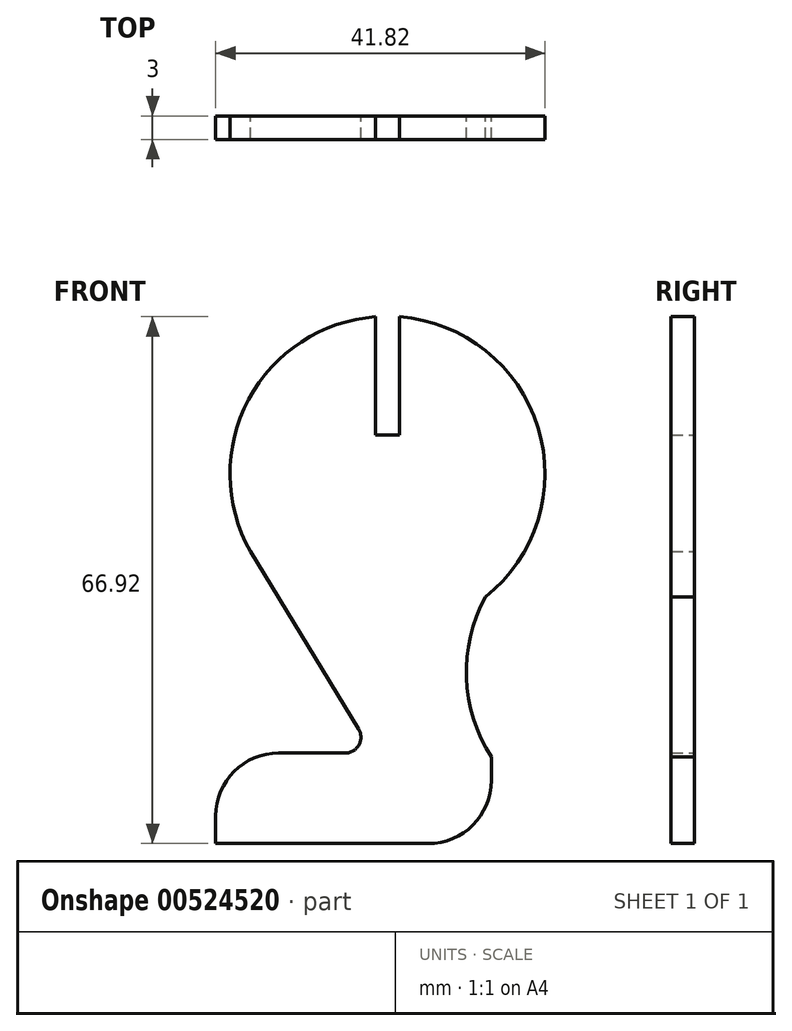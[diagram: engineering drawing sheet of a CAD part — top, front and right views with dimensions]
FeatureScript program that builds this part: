
annotation { "Feature Type Name" : "Feature", "Feature Type Description" : "" }
export const myFeature = defineFeature(function(context is Context, id is Id, definition is map)
    precondition{}
    {
        {
            var Q0;
            Q0=qCreatedBy(makeId("Front.planeOp"),FACE);
            var sketch = newSketch(context, id + "F0", { "sketchPlane" : qUnion([Q0])});
            skArc(sketch, "E0", {"start": v(-30.12, 41.93) * mm, "mid": v(-46.55, 30.84) * mm, "end": v(-45.37, 11.06) * mm});
            skLineSegment(sketch, "E1", {"start": v(-30.12, 41.93) * mm, "end": v(-30.12, 26.93) * mm});
            skLineSegment(sketch, "E2", {"start": v(-30.12, 26.93) * mm, "end": v(-27.12, 26.93) * mm});
            skLineSegment(sketch, "E3", {"start": v(-27.12, 26.93) * mm, "end": v(-27.12, 41.93) * mm});
            skLineSegment(sketch, "E4", {"start": v(-46.03, 12.13) * mm, "end": v(-32.29, -10.46) * mm});
            skArc(sketch, "E5", {"start": v(-16.2, 6.32) * mm, "mid": v(-18.59, -3.94) * mm, "end": v(-15.44, -14) * mm});
            skLineSegment(sketch, "E6", {"start": v(-15.44, -14) * mm, "end": v(-15.44, -17) * mm});
            skLineSegment(sketch, "E7", {"start": v(-23.44, -25) * mm, "end": v(-50.44, -25) * mm});
            skLineSegment(sketch, "E8", {"start": v(-50.44, -25) * mm, "end": v(-50.44, -21.5) * mm});
            skLineSegment(sketch, "E9", {"start": v(-42.44, -13.5) * mm, "end": v(-34, -13.5) * mm});
            skPoint(sketch, "E10.visualSharp", {"position": v(-30.44, -13.5) * mm});
            skArc(sketch, "E10.filletArc", {"start": v(-34, -13.5) * mm, "mid": v(-32.25, -12.48) * mm, "end": v(-32.29, -10.46) * mm});
            skPoint(sketch, "E11.visualSharp", {"position": v(-50.44, -13.5) * mm});
            skArc(sketch, "E11.filletArc", {"start": v(-42.44, -13.5) * mm, "mid": v(-48.1, -15.84) * mm, "end": v(-50.44, -21.5) * mm});
            skPoint(sketch, "E12.visualSharp", {"position": v(-15.44, -25) * mm});
            skArc(sketch, "E12.filletArc", {"start": v(-23.44, -25) * mm, "mid": v(-17.78, -22.65) * mm, "end": v(-15.44, -17) * mm});
            skArc(sketch, "E13.trimOffspring", {"start": v(-16.2, 6.32) * mm, "mid": v(-9.5, 27.85) * mm, "end": v(-27.12, 41.93) * mm});
            skSolve(sketch);
        }
        {
            var Q0;
            {var subQ5=sQuery(id+"F0.wireOp",EDGE,"E1");Q0=makeQuery(id+"F0.imprint","IMPRINT",FACE,{"disambiguationData":[TD([[makeQuery(id+"F0.imprint","IMPRINT",EDGE,{"derivedFrom":subQ5}),-1.0]])]});}
            var Q1;
            {var subQ0=sQuery(id+"F0.wireOp",EDGE,"E4");var subQ1=sQuery(id+"F0.wireOp",EDGE,"E0");var subQ2=makeQuery(id+"F0.imprint","INTERSECT",VERTEX,{"disambiguationData":[OD(0.0)],"derivedFrom":[subQ1,subQ0]});Q1=makeQuery(id+"F0.imprint","IMPRINT",FACE,{"disambiguationData":[TD([[makeQuery(id+"F0.imprint","IMPRINT",EDGE,{"disambiguationData":[TD([[subQ2,1.0]])],"derivedFrom":subQ1}),1.0]])]});}
            extrude(context, id + "F1", {"entities" : qUnion([Q0, Q1]), "depth" : 3 * mm, "offsetDistance" : 25 * mm});
        }
    });
